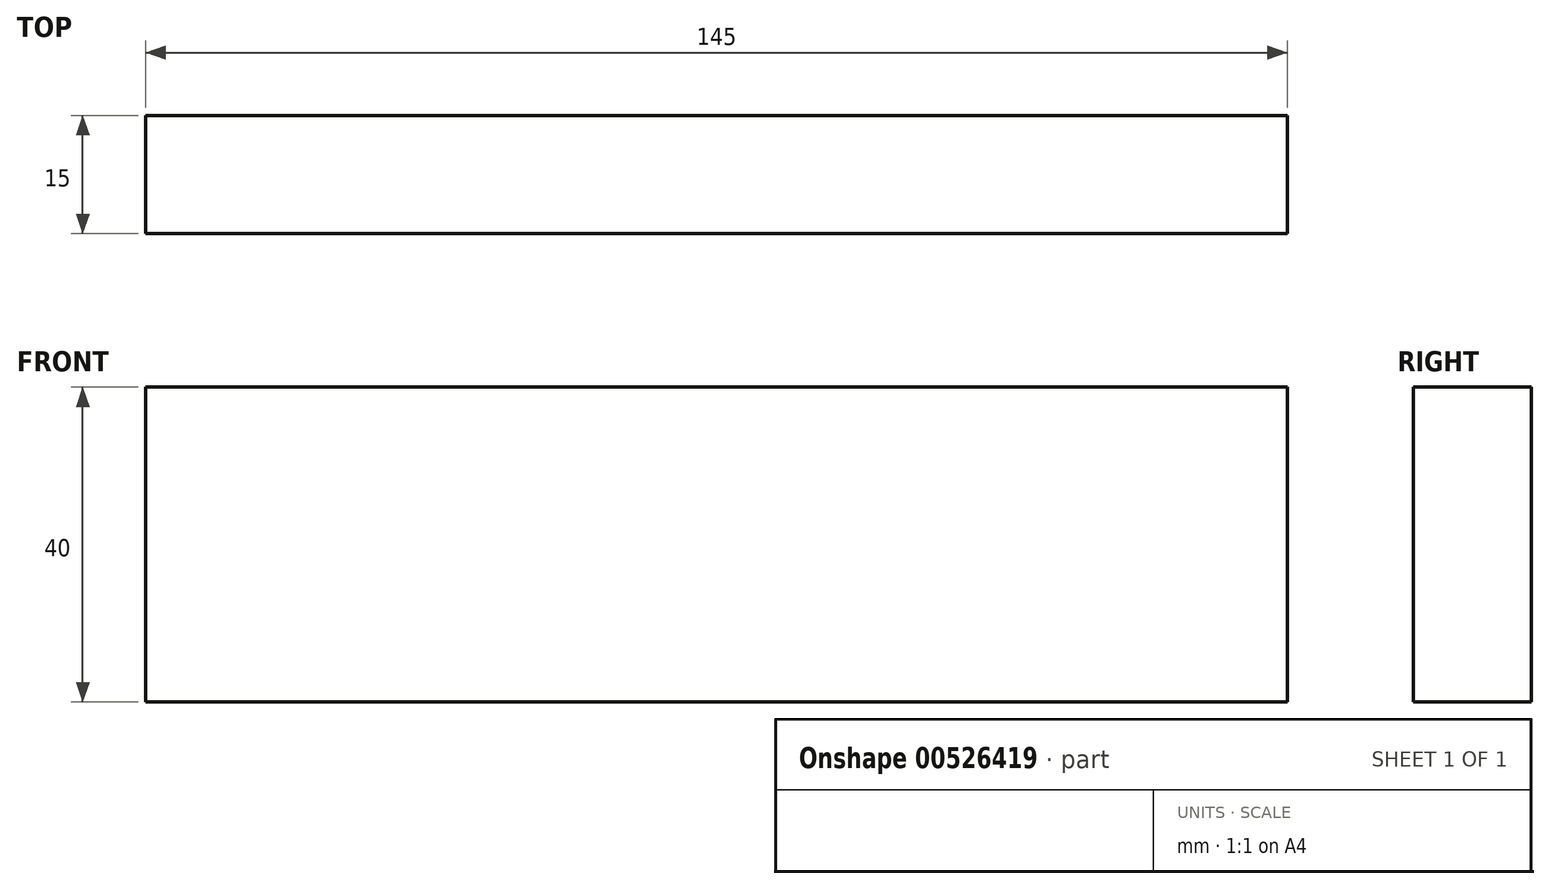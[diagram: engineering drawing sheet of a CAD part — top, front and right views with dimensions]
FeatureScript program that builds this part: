
annotation { "Feature Type Name" : "Feature", "Feature Type Description" : "" }
export const myFeature = defineFeature(function(context is Context, id is Id, definition is map)
    precondition{}
    {
        {
            var Q0;
            Q0=qCreatedBy(makeId("Front.planeOp"),FACE);
            var sketch = newSketch(context, id + "F0", { "sketchPlane" : qUnion([Q0])});
            skLineSegment(sketch, "E0.bottom", {"start": v(0, 0) * mm, "end": v(145, 0) * mm});
            skLineSegment(sketch, "E0.top", {"start": v(0, 40) * mm, "end": v(145, 40) * mm});
            skLineSegment(sketch, "E0.left", {"start": v(0, 0) * mm, "end": v(0, 40) * mm});
            skLineSegment(sketch, "E0.right", {"start": v(145, 0) * mm, "end": v(145, 40) * mm});
            skSolve(sketch);
        }
        {
            var Q0;
            Q0 = qSketchRegion(id + "F0", true);
            extrude(context, id + "F1", {"entities" : qUnion([Q0]), "depth" : 15 * mm, "offsetDistance" : 25 * mm});
        }
    });
